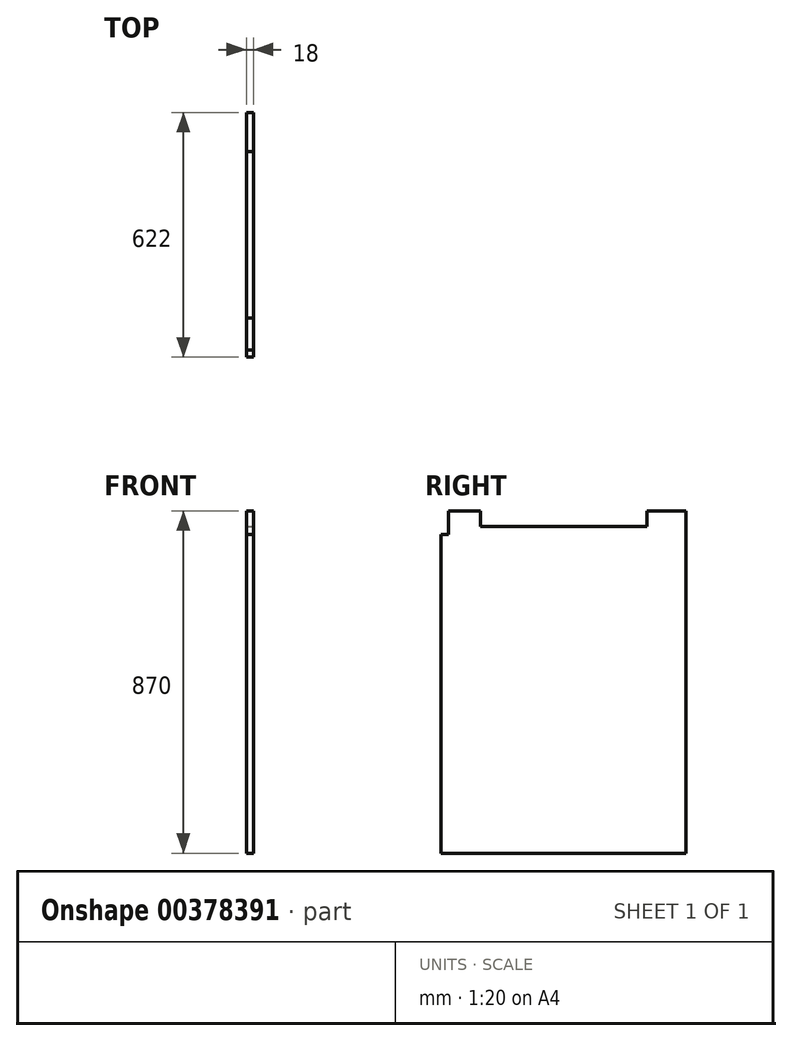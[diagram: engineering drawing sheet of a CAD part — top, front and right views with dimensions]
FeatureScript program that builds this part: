
annotation { "Feature Type Name" : "Feature", "Feature Type Description" : "" }
export const myFeature = defineFeature(function(context is Context, id is Id, definition is map)
    precondition{}
    {
        {
            var Q0;
            Q0=qCreatedBy(makeId("Right.planeOp"),FACE);
            var sketch = newSketch(context, id + "F0", { "sketchPlane" : qUnion([Q0])});
            skLineSegment(sketch, "E0.bottom", {"start": v(311, 435) * mm, "end": v(-311, 435) * mm});
            skLineSegment(sketch, "E0.top", {"start": v(311, -435) * mm, "end": v(-311, -435) * mm});
            skLineSegment(sketch, "E0.left", {"start": v(311, 435) * mm, "end": v(311, -435) * mm});
            skLineSegment(sketch, "E0.right", {"start": v(-311, 435) * mm, "end": v(-311, -435) * mm});
            skPoint(sketch, "E0.middle", {"position": v(0, 0) * mm});
            skSolve(sketch);
        }
        {
            var Q0;
            Q0=qSketchRegion(id+"F0",true);
            extrude(context, id + "F1", {"entities" : qUnion([Q0]), "depth" : 18 * mm});
        }
        {
            var Q0;
            Q0=makeQuery(id+"F1.opExtrude","CAP_FACE",FACE,{"disambiguationData":[OSD([sQuery(id+"F0.wireOp",EDGE,"E0.bottom"),sQuery(id+"F0.wireOp",EDGE,"E0.top"),sQuery(id+"F0.wireOp",EDGE,"E0.left"),sQuery(id+"F0.wireOp",EDGE,"E0.right")])],"isStart":false});
            var sketch = newSketch(context, id + "F2", { "sketchPlane" : qUnion([Q0])});
            skLineSegment(sketch, "E1.bottom", {"start": v(-311, 435) * mm, "end": v(-293, 435) * mm});
            skLineSegment(sketch, "E1.top", {"start": v(-311, 375) * mm, "end": v(-293, 375) * mm});
            skLineSegment(sketch, "E1.left", {"start": v(-311, 435) * mm, "end": v(-311, 375) * mm});
            skLineSegment(sketch, "E1.right", {"start": v(-293, 435) * mm, "end": v(-293, 375) * mm});
            skLineSegment(sketch, "E2.bottom", {"start": v(-211, 435) * mm, "end": v(211, 435) * mm});
            skLineSegment(sketch, "E2.top", {"start": v(-211, 395) * mm, "end": v(211, 395) * mm});
            skLineSegment(sketch, "E2.left", {"start": v(-211, 435) * mm, "end": v(-211, 395) * mm});
            skLineSegment(sketch, "E2.right", {"start": v(211, 435) * mm, "end": v(211, 395) * mm});
            skSolve(sketch);
        }
        {
            var Q0;
            Q0 = qSketchRegion(id + "F2", true);
            extrude(context, id + "F3", {"entities" : qUnion([Q0]), "operationType" : NewBodyOperationType.REMOVE, "oppositeDirection" : true, "depth" : 18 * mm});
        }
    });
